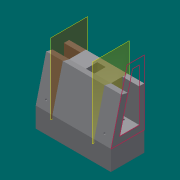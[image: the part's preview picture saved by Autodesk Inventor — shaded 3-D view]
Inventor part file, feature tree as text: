
AUTODESK INVENTOR PART (.ipt)
format: ipt  version: 2013 (Build 170138000, 138)  size: 196,608 bytes
history: native  units: mm
features: sketch x9, extrude x7, other x4, hole x2, mirror x1
ambient origin geometry x8: Origin, YZ Plane, XZ Plane, XY Plane, X Axis, Y Axis, Z Axis, Center Point
feature tree (23):
  other  "ソリッド1"
  extrude  "押し出し1"  Depth=80.0mm
  hole  "穴1"  [1 undecoded]
  other  "作業平面1"
  extrude  "押し出し4"  TaperAngle=15.0deg  [1 undecoded]
  mirror  "ミラー1"
  hole  "穴3"  [1 undecoded]
  sketch  "スケッチ7"
  other  "作業平面2"
  extrude  "押し出し5"  Depth=10.0mm
  other  "作業平面3"
  extrude  "押し出し6"  Depth=10.0mm
  extrude  "押し出し7"  Depth=10.0mm
  extrude  "押し出し8"  Depth=10.0mm
  extrude  "押し出し9"  Depth=10.0mm
  sketch  "スケッチ1"
  sketch  "スケッチ2"
  sketch  "スケッチ6"
  sketch  "スケッチ8"
  sketch  "スケッチ9"
  sketch  "スケッチ10"
  sketch  "スケッチ11"
  sketch  "スケッチ12"
note: 3 required parameter values undecoded (feature->parameter linkage not recoverable at this tier; creation-order binding heuristic only, values carry confidence <= 0.55)
